# Revit family: Accessory-Tissue_Holder-KALLISTA-Vice-P34603_1
name_source: partatom
category: Specialty Equipment
units: mm (PartAtom-declared; Revit-internal decimal feet)

## family parameters
Cut with Voids When Loaded = No
Host = Face
OmniClass Number = 23.31.25.21
OmniClass Title = Toilet Paper Dispensers
Part Type = Normal
Room Calculation Point = No
Round Connector Dimension = Use Diameter
Shared = No

## types (5) — shared parameters
ADA Compliant = No
Assembly Code = C1030200
Date Modified = 4/30/2024
Default Elevation = 42"
Description = To Let Paper Holder
Height = 2 1/4"
Length = 7 1/16"
Manufacturer = Kallista Co.
Master Format 2014 = 10 28 00
Master Format 2014 Name = Toilet, Bath, and Laundry Accessories
Material = Premium Metal Construction
Product Name = Vice
URL = https://www.kallista.com
WaterSense Certified = No
Width = 4"

## per-type parameters (varying)
| type | Finish | Model | Secondary Finish | Type |
| Brushed French Gold, AF-French Gold | Kallista-Metal-AF-French_Gold | P34603-BAF-AF | Kallista-Metal-BAF-Brushed_French_Gold | 1 |
| Brushed Nickel, BGP | Kallista-Metal-BGP | P34603-BN-BGP | Kallista-Metal-BN-Brushed_Nickel | 2 |
| Brushed Nickel, SN-Polished Nickel | Kallista-Metal-SN-Polished_Nickel | P34603-BN-SN | Kallista-Metal-BN-Brushed_Nickel | 3 |
| Brushed Bronze, CP-Chrome | Kallista-Metal-CP-Chrome | P34603-BV-CP | Kallista-Metal-BV-Brushed_Bronze | 4 |
| Chrome, CP-Chrome | Kallista-Metal-CP-Chrome | P34603-CP-CP | Kallista-Metal-CP-Chrome | 5 |

## geometry (parser evidence)
native form markers: Sweep x6
no freeform markers — native parametric forms only
